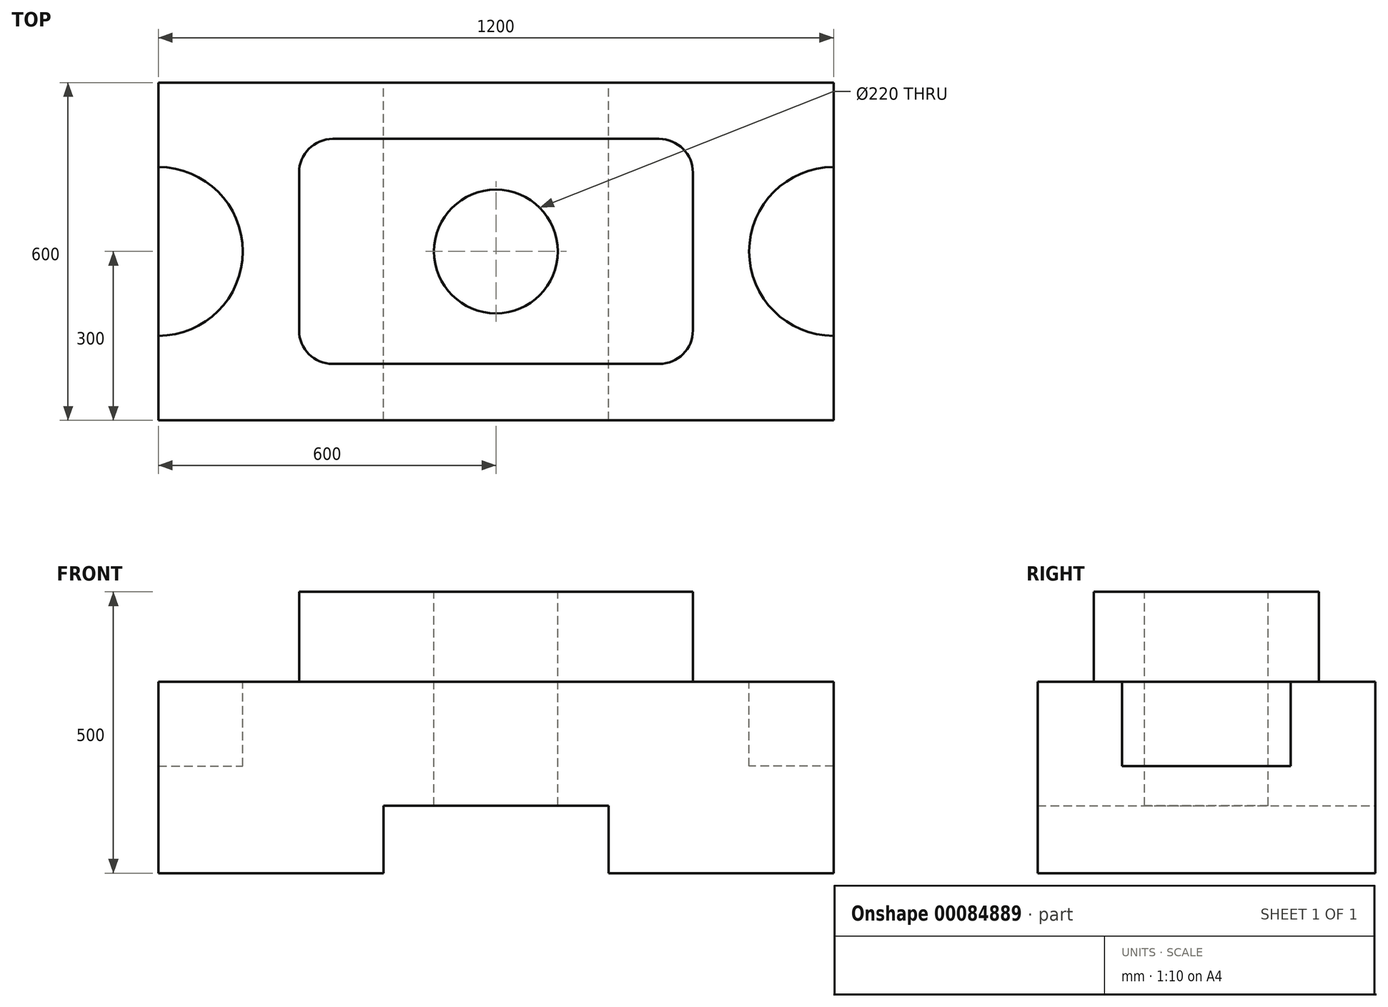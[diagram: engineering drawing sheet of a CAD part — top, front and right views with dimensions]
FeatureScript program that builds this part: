
annotation { "Feature Type Name" : "Feature", "Feature Type Description" : "" }
export const myFeature = defineFeature(function(context is Context, id is Id, definition is map)
    precondition{}
    {
        {
            var Q0;
            Q0=qCreatedBy(makeId("Front.planeOp"),FACE);
            var sketch = newSketch(context, id + "F0", { "sketchPlane" : qUnion([Q0])});
            skLineSegment(sketch, "E0.bottom", {"start": v(-600, -508.73) * mm, "end": v(-200, -508.73) * mm});
            skLineSegment(sketch, "E0.top", {"start": v(-600, -168.73) * mm, "end": v(600, -168.73) * mm});
            skLineSegment(sketch, "E0.left", {"start": v(-600, -508.73) * mm, "end": v(-600, -168.73) * mm});
            skLineSegment(sketch, "E0.right", {"start": v(600, -508.73) * mm, "end": v(600, -168.73) * mm});
            skPoint(sketch, "E0.middle", {"position": v(0, -338.73) * mm});
            skLineSegment(sketch, "E1.top", {"start": v(-200, -388.73) * mm, "end": v(200, -388.73) * mm});
            skLineSegment(sketch, "E1.left", {"start": v(-200, -508.73) * mm, "end": v(-200, -388.73) * mm});
            skLineSegment(sketch, "E1.right", {"start": v(200, -508.73) * mm, "end": v(200, -388.73) * mm});
            skPoint(sketch, "E1.middle", {"position": v(0, -508.73) * mm});
            skLineSegment(sketch, "E2.trimOffspring", {"start": v(200, -508.73) * mm, "end": v(600, -508.73) * mm});
            skPoint(sketch, "E3.orphan", {"position": v(200, -628.73) * mm});
            skPoint(sketch, "E4.orphan", {"position": v(-200, -628.73) * mm});
            skSolve(sketch);
        }
        {
            var Q0;
            Q0 = qSketchRegion(id + "F0", true);
            extrude(context, id + "F1", {"entities" : qUnion([Q0]), "depth" : 600 * mm});
        }
        {
            var Q0;
            Q0=makeQuery(id+"F1.opExtrude","SWEPT_FACE",FACE,{"disambiguationData":[OSD([sQuery(id+"F0.wireOp",EDGE,"E0.top")])]});
            var sketch = newSketch(context, id + "F2", { "sketchPlane" : qUnion([Q0])});
            skLineSegment(sketch, "E5.bottom", {"start": v(-290, -500) * mm, "end": v(290, -500) * mm});
            skLineSegment(sketch, "E5.top", {"start": v(-290, -100) * mm, "end": v(290, -100) * mm});
            skLineSegment(sketch, "E5.left", {"start": v(-350, -440) * mm, "end": v(-350, -160) * mm});
            skLineSegment(sketch, "E5.right", {"start": v(350, -440) * mm, "end": v(350, -160) * mm});
            skPoint(sketch, "E5.middle", {"position": v(0, -300) * mm});
            skPoint(sketch, "E5.middle.positionSnap0", {"position": v(600, -300) * mm});
            skPoint(sketch, "E5.middle.positionSnap1", {"position": v(0, 0) * mm});
            skPoint(sketch, "E5.centerSnap0", {"position": v(600, -300) * mm});
            skPoint(sketch, "E5.centerSnap1", {"position": v(0, 0) * mm});
            skPoint(sketch, "E6.visualSharp", {"position": v(-350, -100) * mm});
            skArc(sketch, "E6.filletArc", {"start": v(-290, -100) * mm, "mid": v(-332.43, -117.57) * mm, "end": v(-350, -160) * mm});
            skPoint(sketch, "E7.visualSharp", {"position": v(350, -500) * mm});
            skArc(sketch, "E7.filletArc", {"start": v(290, -500) * mm, "mid": v(332.43, -482.43) * mm, "end": v(350, -440) * mm});
            skPoint(sketch, "E8.visualSharp", {"position": v(-350, -500) * mm});
            skArc(sketch, "E8.filletArc", {"start": v(-350, -440) * mm, "mid": v(-332.43, -482.43) * mm, "end": v(-290, -500) * mm});
            skPoint(sketch, "E9.visualSharp", {"position": v(350, -100) * mm});
            skArc(sketch, "E9.filletArc", {"start": v(350, -160) * mm, "mid": v(332.43, -117.57) * mm, "end": v(290, -100) * mm});
            skSolve(sketch);
        }
        {
            var Q0;
            Q0 = qSketchRegion(id + "F2", true);
            extrude(context, id + "F3", {"entities" : qUnion([Q0]), "operationType" : NewBodyOperationType.ADD, "depth" : 160 * mm});
        }
        {
            var Q0;
            Q0=makeQuery(id+"F3.opExtrude","CAP_FACE",FACE,{"disambiguationData":[OSD([sQuery(id+"F2.wireOp",EDGE,"E5.bottom"),sQuery(id+"F2.wireOp",EDGE,"E5.top"),sQuery(id+"F2.wireOp",EDGE,"E5.left"),sQuery(id+"F2.wireOp",EDGE,"E5.right"),sQuery(id+"F2.wireOp",EDGE,"E6.filletArc"),sQuery(id+"F2.wireOp",EDGE,"E7.filletArc"),sQuery(id+"F2.wireOp",EDGE,"E8.filletArc"),sQuery(id+"F2.wireOp",EDGE,"E9.filletArc")])],"isStart":false});
            var sketch = newSketch(context, id + "F4", { "sketchPlane" : qUnion([Q0])});
            skCircle(sketch, "E10", {"center": v(0, -300) * mm, "radius": 110 * mm});
            skPoint(sketch, "E10.centerSnap0", {"position": v(350, -300) * mm});
            skSolve(sketch);
        }
        {
            var Q0;
            Q0 = qSketchRegion(id + "F4", true);
            extrude(context, id + "F5", {"entities" : qUnion([Q0]), "operationType" : NewBodyOperationType.REMOVE, "endBound" : BoundingType.THROUGH_ALL, "oppositeDirection" : true, "depth" : 25 * mm});
        }
        {
            var Q0;
            Q0=makeQuery(id+"F1.opExtrude","SWEPT_FACE",FACE,{"disambiguationData":[OSD([sQuery(id+"F0.wireOp",EDGE,"E0.top")])]});
            var sketch = newSketch(context, id + "F6", { "sketchPlane" : qUnion([Q0])});
            skArc(sketch, "E11", {"start": v(-600, -450) * mm, "mid": v(-450, -300) * mm, "end": v(-600, -150) * mm});
            skLineSegment(sketch, "E12", {"start": v(-600, -150) * mm, "end": v(-600, -450) * mm});
            skArc(sketch, "E13", {"start": v(600, -150) * mm, "mid": v(450, -300) * mm, "end": v(600, -450) * mm});
            skLineSegment(sketch, "E14", {"start": v(600, -450) * mm, "end": v(600, -150) * mm});
            skSolve(sketch);
        }
        {
            var Q0;
            Q0 = qSketchRegion(id + "F6", true);
            extrude(context, id + "F7", {"entities" : qUnion([Q0]), "operationType" : NewBodyOperationType.REMOVE, "oppositeDirection" : true, "depth" : 150 * mm});
        }
    });
